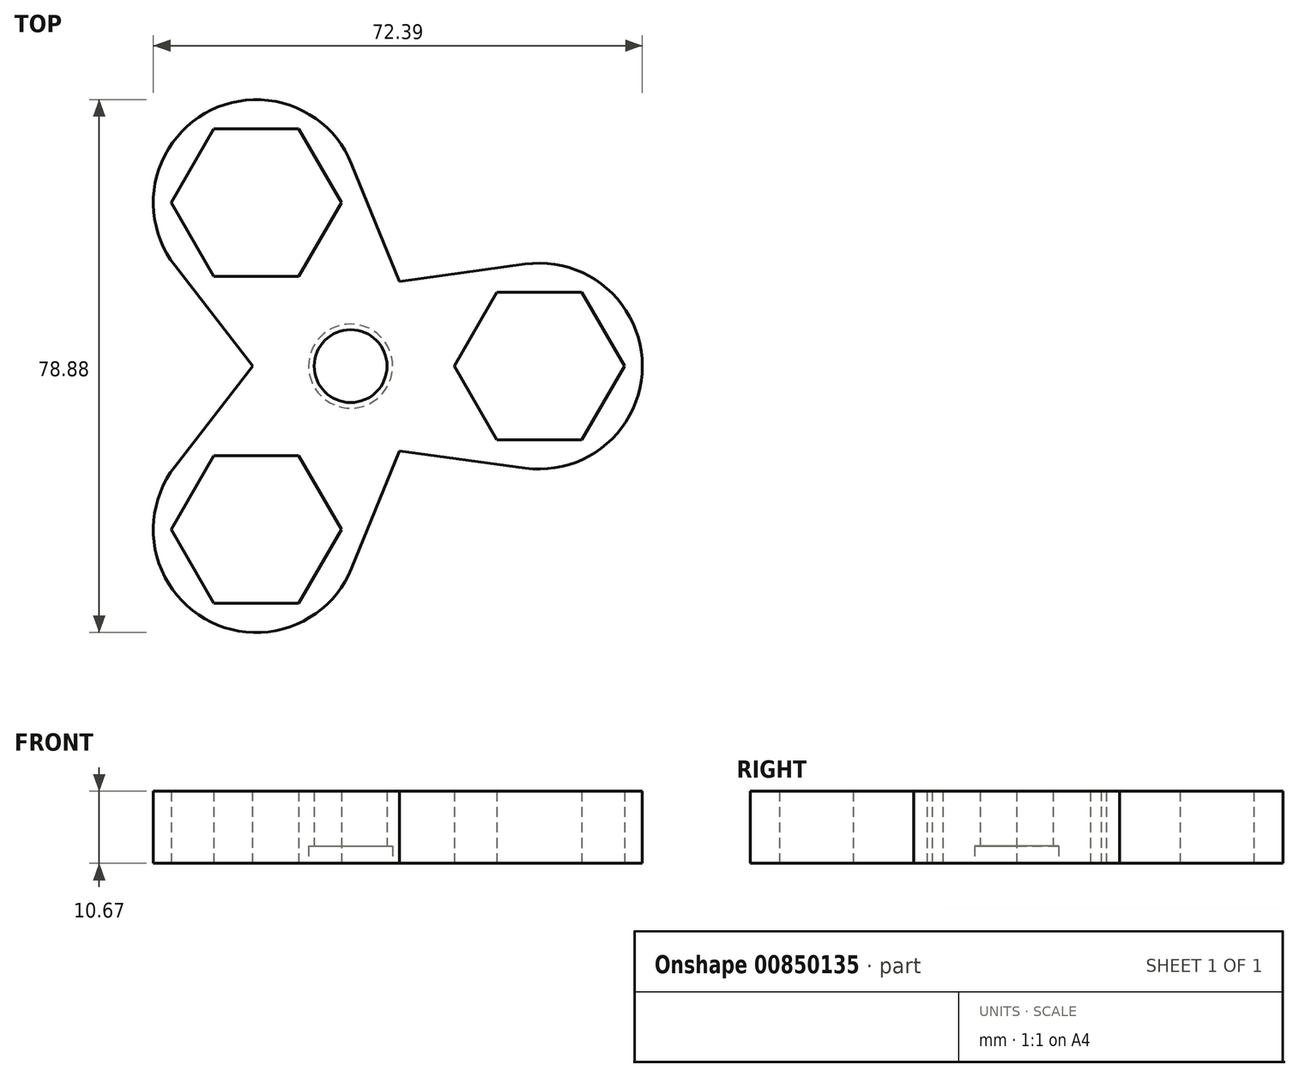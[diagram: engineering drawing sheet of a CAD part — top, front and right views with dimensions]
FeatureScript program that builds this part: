
annotation { "Feature Type Name" : "Feature", "Feature Type Description" : "" }
export const myFeature = defineFeature(function(context is Context, id is Id, definition is map)
    precondition{}
    {
        {
            var Q0;
            Q0=qCreatedBy(makeId("Top.planeOp"),FACE);
            var sketch = newSketch(context, id + "F0", { "sketchPlane" : qUnion([Q0])});
            skCircle(sketch, "E0", {"center": v(0, 0) * mm, "radius": 11.43 * mm});
            skCircle(sketch, "E1", {"center": v(27.94, 0) * mm, "radius": 15.24 * mm});
            skLineSegment(sketch, "E2", {"start": v(-1.56, 11.32) * mm, "end": v(25.86, 15.1) * mm});
            skLineSegment(sketch, "E3", {"start": v(-1.56, -11.32) * mm, "end": v(25.86, -15.1) * mm});
            skCircle(sketch, "E4.cCircle", {"center": v(27.94, 0) * mm, "radius": 10.92 * mm, "construction": true});
            skLineSegment(sketch, "E4.0", {"start": v(34.25, -10.92) * mm, "end": v(21.63, -10.92) * mm});
            skLineSegment(sketch, "E4.1", {"start": v(21.63, -10.92) * mm, "end": v(15.33, 0) * mm});
            skLineSegment(sketch, "E4.2", {"start": v(15.33, 0) * mm, "end": v(21.63, 10.92) * mm});
            skLineSegment(sketch, "E4.3", {"start": v(21.63, 10.92) * mm, "end": v(34.25, 10.92) * mm});
            skLineSegment(sketch, "E4.4", {"start": v(34.25, 10.92) * mm, "end": v(40.55, 0) * mm});
            skLineSegment(sketch, "E4.5", {"start": v(40.55, 0) * mm, "end": v(34.25, -10.92) * mm});
            skPoint(sketch, "E4.0.midPoint", {"position": v(27.94, -10.92) * mm});
            skSolve(sketch);
        }
        {
            var Q0;
            {var subQ0=sQuery(id+"F0.wireOp",EDGE,"E2");Q0=makeQuery(id+"F0.imprint","IMPRINT",FACE,{"disambiguationData":[TD([[makeQuery(id+"F0.imprint","IMPRINT",EDGE,{"derivedFrom":subQ0}),-1.0]])]});}
            var Q1;
            {var subQ0=sQuery(id+"F0.wireOp",EDGE,"E0");var subQ1=makeQuery(id+"F0.imprint","INTERSECT",VERTEX,{"derivedFrom":[subQ0,sQuery(id+"F0.wireOp",EDGE,"E2")]});Q1=makeQuery(id+"F0.imprint","IMPRINT",FACE,{"disambiguationData":[TD([[makeQuery(id+"F0.imprint","IMPRINT",EDGE,{"disambiguationData":[TD([[subQ1,-1.0]])],"derivedFrom":subQ0}),1.0]])]});}
            var Q2;
            {var subQ0=sQuery(id+"F0.wireOp",EDGE,"E1");var subQ1=makeQuery(id+"F0.imprint","INTERSECT",VERTEX,{"derivedFrom":[subQ0,sQuery(id+"F0.wireOp",EDGE,"E2")]});Q2=makeQuery(id+"F0.imprint","IMPRINT",FACE,{"disambiguationData":[TD([[makeQuery(id+"F0.imprint","IMPRINT",EDGE,{"disambiguationData":[TD([[subQ1,-1.0]])],"derivedFrom":subQ0}),1.0]])]});}
            extrude(context, id + "F1", {"entities" : qUnion([Q0, Q1, Q2]), "depth" : 10.67 * mm, "offsetDistance" : 25.4 * mm});
        }
        {
            var Q0;
            Q0=makeQuery(id+"F1.opExtrude","CAP_FACE",FACE,{"disambiguationData":[OSD([sQuery(id+"F0.wireOp",EDGE,"E0"),sQuery(id+"F0.wireOp",EDGE,"E1"),sQuery(id+"F0.wireOp",EDGE,"E2"),sQuery(id+"F0.wireOp",EDGE,"E3")])],"isStart":false});
            var sketch = newSketch(context, id + "F2", { "sketchPlane" : qUnion([Q0])});
            skCircle(sketch, "E5", {"center": v(0, 0) * mm, "radius": 11.43 * mm, "construction": true});
            skSolve(sketch);
        }
        {
            var Q0;
            Q0=makeQuery(id+"F1.opExtrude","SWEPT_BODY",BODY,{"disambiguationData":[OSD([sQuery(id+"F0.wireOp",EDGE,"E0"),sQuery(id+"F0.wireOp",EDGE,"E1"),sQuery(id+"F0.wireOp",EDGE,"E2"),sQuery(id+"F0.wireOp",EDGE,"E3")])]});
            var Q1;
            Q1=sQuery(id+"F2.wireOp",EDGE,"E5");
            circularPattern(context, id + "F3", {"operationType" : NewBodyOperationType.ADD, "entities" : qUnion([Q0]), "axis" : qUnion([Q1]), "angle" : 360 * degree, "instanceCount" : 3, "equalSpace" : true});
        }
        {
            var Q0;
            {var subQ0=makeQuery(id+"F1.opExtrude","CAP_FACE",FACE,{"disambiguationData":[OSD([sQuery(id+"F0.wireOp",EDGE,"E0"),sQuery(id+"F0.wireOp",EDGE,"E1"),sQuery(id+"F0.wireOp",EDGE,"E2"),sQuery(id+"F0.wireOp",EDGE,"E3"),sQuery(id+"F0.wireOp",EDGE,"E4.0"),sQuery(id+"F0.wireOp",EDGE,"E4.1"),sQuery(id+"F0.wireOp",EDGE,"E4.2"),sQuery(id+"F0.wireOp",EDGE,"E4.3"),sQuery(id+"F0.wireOp",EDGE,"E4.4"),sQuery(id+"F0.wireOp",EDGE,"E4.5")])],"isStart":true});Q0=makeQuery(id+"F3.boolean.opBoolean","MERGE",FACE,{"derivedFrom":[subQ0,makeQuery(id+"F3.opPattern","COPY",FACE,{"derivedFrom":subQ0,"instanceName":"1"}),makeQuery(id+"F3.opPattern","COPY",FACE,{"derivedFrom":subQ0,"instanceName":"2"})]});}
            var sketch = newSketch(context, id + "F4", { "sketchPlane" : qUnion([Q0])});
            skCircle(sketch, "E6", {"center": v(0, 0) * mm, "radius": 6.22 * mm});
            skSolve(sketch);
        }
        {
            var Q0;
            Q0=makeQuery(id+"F4.imprint","IMPRINT",FACE,{"disambiguationData":[TD([[makeQuery(id+"F4.imprint","IMPRINT",EDGE,{"derivedFrom":sQuery(id+"F4.wireOp",EDGE,"E6")}),1.0]])]});
            extrude(context, id + "F5", {"entities" : qUnion([Q0]), "operationType" : NewBodyOperationType.REMOVE, "oppositeDirection" : true, "depth" : 2.54 * mm, "offsetDistance" : 25.4 * mm});
        }
        {
            var Q0;
            Q0=makeQuery(id+"F5.boolean.opBoolean","COPY",FACE,{"derivedFrom":makeQuery(id+"F5.opExtrude","CAP_FACE",FACE,{"disambiguationData":[OSD([sQuery(id+"F4.wireOp",EDGE,"E6")])],"isStart":false})});
            var sketch = newSketch(context, id + "F6", { "sketchPlane" : qUnion([Q0])});
            skCircle(sketch, "E7", {"center": v(0, 0) * mm, "radius": 5.4 * mm});
            skSolve(sketch);
        }
        {
            var Q0;
            Q0=makeQuery(id+"F6.imprint","IMPRINT",FACE,{"disambiguationData":[TD([[makeQuery(id+"F6.imprint","IMPRINT",EDGE,{"derivedFrom":sQuery(id+"F6.wireOp",EDGE,"E7")}),1.0]])]});
            extrude(context, id + "F7", {"entities" : qUnion([Q0]), "operationType" : NewBodyOperationType.REMOVE, "oppositeDirection" : true, "depth" : 25.4 * mm, "offsetDistance" : 25.4 * mm});
        }
    });
